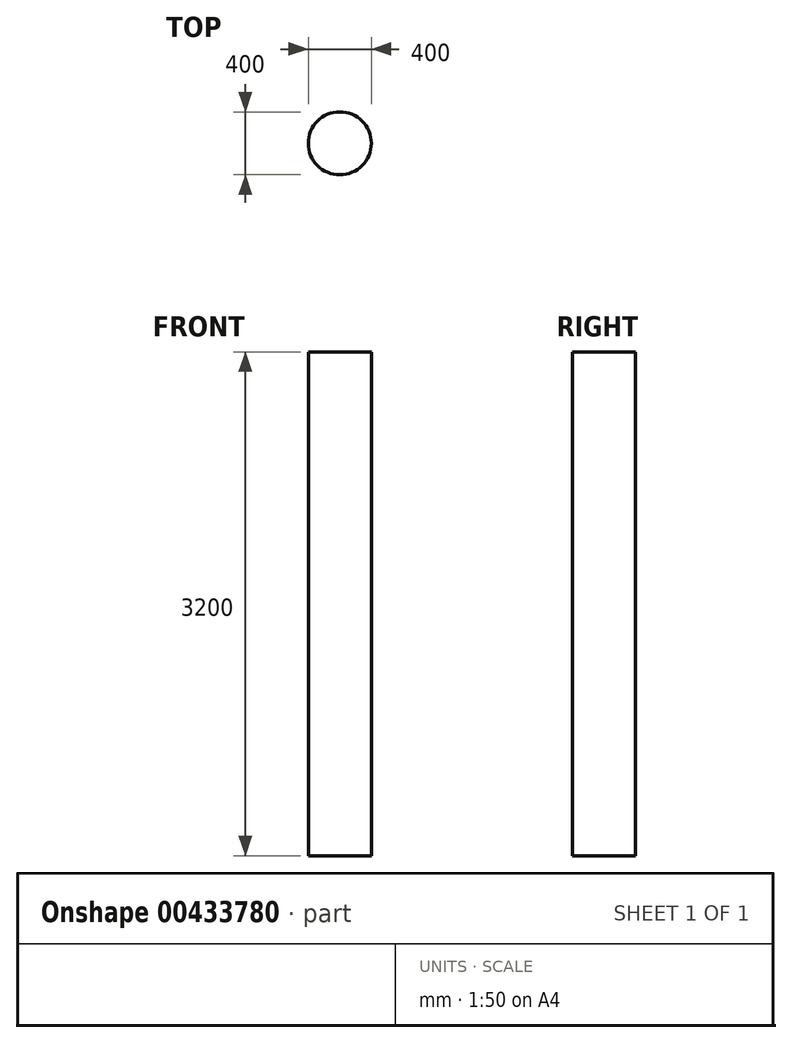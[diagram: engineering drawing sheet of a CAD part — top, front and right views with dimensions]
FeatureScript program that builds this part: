
annotation { "Feature Type Name" : "Feature", "Feature Type Description" : "" }
export const myFeature = defineFeature(function(context is Context, id is Id, definition is map)
    precondition{}
    {
        {
            var Q0;
            Q0=qCreatedBy(makeId("Top.planeOp"),FACE);
            var sketch = newSketch(context, id + "F0", { "sketchPlane" : qUnion([Q0])});
            skCircle(sketch, "E0", {"center": v(-1400, 0) * mm, "radius": 200 * mm});
            skLineSegment(sketch, "E1", {"start": v(0, 0) * mm, "end": v(0, 293.68) * mm, "construction": true});
            skCircle(sketch, "E2.MirrorC", {"center": v(1400, 0) * mm, "radius": 200 * mm});
            skSolve(sketch);
        }
        {
            var Q0;
            Q0=makeQuery(id+"F0.imprint","IMPRINT",FACE,{"disambiguationData":[TD([[makeQuery(id+"F0.imprint","IMPRINT",EDGE,{"derivedFrom":sQuery(id+"F0.wireOp",EDGE,"E0")}),1.0]])]});
            var Q1;
            Q1=makeQuery(id+"F0.imprint","IMPRINT",FACE,{"disambiguationData":[TD([[makeQuery(id+"F0.imprint","IMPRINT",EDGE,{"derivedFrom":sQuery(id+"F0.wireOp",EDGE,"E2.MirrorC")}),-1.0]])]});
            extrude(context, id + "F1", {"entities" : qUnion([Q0, Q1]), "depth" : 3200 * mm});
        }
    });
